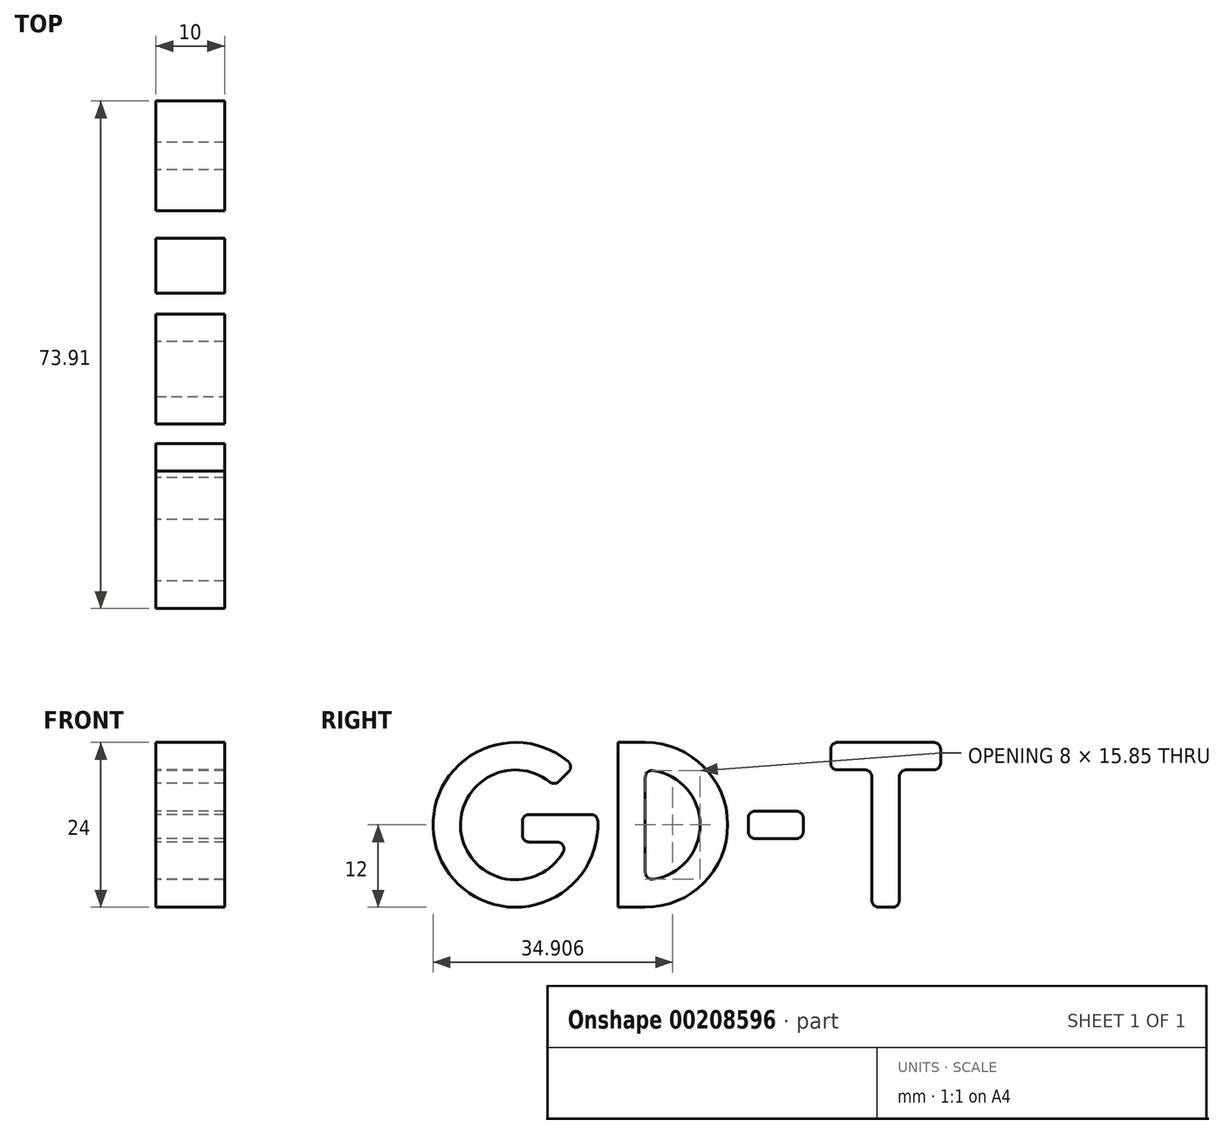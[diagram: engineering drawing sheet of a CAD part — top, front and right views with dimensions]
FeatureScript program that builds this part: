
annotation { "Feature Type Name" : "Feature", "Feature Type Description" : "" }
export const myFeature = defineFeature(function(context is Context, id is Id, definition is map)
    precondition{}
    {
        {
            var Q0;
            Q0=qCreatedBy(makeId("Right.planeOp"),FACE);
            var sketch = newSketch(context, id + "F0", { "sketchPlane" : qUnion([Q0])});
            skArc(sketch, "E0", {"start": v(20.49, 20.49) * mm, "mid": v(1.22, 6.72) * mm, "end": v(23.9, 13.5) * mm});
            skLineSegment(sketch, "E1", {"start": v(23.9, 13.5) * mm, "end": v(13, 13.5) * mm});
            skLineSegment(sketch, "E2", {"start": v(13, 13.5) * mm, "end": v(13, 9.5) * mm});
            skLineSegment(sketch, "E3", {"start": v(13, 9.5) * mm, "end": v(19.6, 9.5) * mm});
            skArc(sketch, "E4", {"start": v(17.66, 17.66) * mm, "mid": v(4.22, 10.15) * mm, "end": v(19.6, 9.5) * mm});
            skLineSegment(sketch, "E5", {"start": v(17.66, 17.66) * mm, "end": v(20.49, 20.49) * mm});
            skArc(sketch, "E6", {"start": v(30.9, 0) * mm, "mid": v(42.9, 12) * mm, "end": v(30.9, 24) * mm});
            skLineSegment(sketch, "E7.bottom", {"start": v(26.9, 0) * mm, "end": v(30.9, 0) * mm});
            skLineSegment(sketch, "E7.top", {"start": v(26.9, 24) * mm, "end": v(30.9, 24) * mm});
            skLineSegment(sketch, "E7.left", {"start": v(26.9, 0) * mm, "end": v(26.9, 24) * mm});
            skArc(sketch, "E8", {"start": v(30.9, 4) * mm, "mid": v(38.9, 12) * mm, "end": v(30.9, 20) * mm});
            skLineSegment(sketch, "E9", {"start": v(30.9, 20) * mm, "end": v(30.9, 4) * mm});
            skLineSegment(sketch, "E10.bottom", {"start": v(45.9, 14) * mm, "end": v(53.9, 14) * mm});
            skLineSegment(sketch, "E10.top", {"start": v(45.9, 10) * mm, "end": v(53.9, 10) * mm});
            skLineSegment(sketch, "E10.left", {"start": v(45.9, 14) * mm, "end": v(45.9, 10) * mm});
            skLineSegment(sketch, "E10.right", {"start": v(53.9, 14) * mm, "end": v(53.9, 10) * mm});
            skLineSegment(sketch, "E11.bottom", {"start": v(57.9, 24) * mm, "end": v(73.9, 24) * mm});
            skLineSegment(sketch, "E11.top", {"start": v(57.9, 20) * mm, "end": v(63.9, 20) * mm});
            skLineSegment(sketch, "E11.left", {"start": v(57.9, 24) * mm, "end": v(57.9, 20) * mm});
            skLineSegment(sketch, "E11.right", {"start": v(73.9, 24) * mm, "end": v(73.9, 20) * mm});
            skLineSegment(sketch, "E12.top", {"start": v(63.9, 0) * mm, "end": v(67.9, 0) * mm});
            skLineSegment(sketch, "E12.left", {"start": v(63.9, 20) * mm, "end": v(63.9, 0) * mm});
            skLineSegment(sketch, "E12.right", {"start": v(67.9, 20) * mm, "end": v(67.9, 0) * mm});
            skLineSegment(sketch, "E13.trimOffspring", {"start": v(67.9, 20) * mm, "end": v(73.9, 20) * mm});
            skSolve(sketch);
        }
        {
            var Q0;
            Q0 = qSketchRegion(id + "F0", true);
            extrude(context, id + "F1", {"entities" : qUnion([Q0]), "depth" : 10 * mm});
        }
        {
            var Q0;
            {var subQ0=sQuery(id+"F0.wireOp",EDGE,"E9");var subQ1=sQuery(id+"F0.wireOp",EDGE,"E8");Q0=makeQuery(id+"F1.opExtrude","SWEPT_EDGE",EDGE,{"disambiguationData":[OSD([subQ1,subQ0]),TDD([makeQuery(id+"F0.imprint","INTERSECT",VERTEX,{"disambiguationData":[OD(1.0)],"derivedFrom":[subQ1,subQ0]})])]});}
            var Q1;
            {var subQ0=sQuery(id+"F0.wireOp",EDGE,"E9");var subQ1=sQuery(id+"F0.wireOp",EDGE,"E8");Q1=makeQuery(id+"F1.opExtrude","SWEPT_EDGE",EDGE,{"disambiguationData":[OSD([subQ1,subQ0]),TDD([makeQuery(id+"F0.imprint","INTERSECT",VERTEX,{"disambiguationData":[OD(0.0)],"derivedFrom":[subQ1,subQ0]})])]});}
            fillet(context, id + "F2", {"entities" : qUnion([Q0, Q1]), "radius" : 1 * mm, "tangentPropagation" : true, "allowEdgeOverflow" : false});
        }
        {
            var Q0;
            Q0=makeQuery(id+"F1.opExtrude","SWEPT_EDGE",EDGE,{"disambiguationData":[OSD([sQuery(id+"F0.wireOp",EDGE,"E3"),sQuery(id+"F0.wireOp",EDGE,"E4")])]});
            var Q1;
            Q1=makeQuery(id+"F1.opExtrude","SWEPT_EDGE",EDGE,{"disambiguationData":[OSD([sQuery(id+"F0.wireOp",EDGE,"E2"),sQuery(id+"F0.wireOp",EDGE,"E3")])]});
            var Q2;
            Q2=makeQuery(id+"F1.opExtrude","SWEPT_EDGE",EDGE,{"disambiguationData":[OSD([sQuery(id+"F0.wireOp",EDGE,"E1"),sQuery(id+"F0.wireOp",EDGE,"E2")])]});
            var Q3;
            Q3=makeQuery(id+"F1.opExtrude","SWEPT_EDGE",EDGE,{"disambiguationData":[OSD([sQuery(id+"F0.wireOp",EDGE,"E0"),sQuery(id+"F0.wireOp",EDGE,"E1")])]});
            var Q4;
            Q4=makeQuery(id+"F1.opExtrude","SWEPT_EDGE",EDGE,{"disambiguationData":[OSD([sQuery(id+"F0.wireOp",EDGE,"E0"),sQuery(id+"F0.wireOp",EDGE,"E5")])]});
            var Q5;
            Q5=makeQuery(id+"F1.opExtrude","SWEPT_EDGE",EDGE,{"disambiguationData":[OSD([sQuery(id+"F0.wireOp",EDGE,"E4"),sQuery(id+"F0.wireOp",EDGE,"E5")])]});
            fillet(context, id + "F3", {"entities" : qUnion([Q0, Q1, Q2, Q3, Q4, Q5]), "radius" : 1 * mm, "tangentPropagation" : true, "allowEdgeOverflow" : false});
        }
        {
            var Q0;
            Q0=makeQuery(id+"F1.opExtrude","SWEPT_EDGE",EDGE,{"disambiguationData":[OSD([sQuery(id+"F0.wireOp",EDGE,"E10.bottom"),sQuery(id+"F0.wireOp",EDGE,"E10.right")])]});
            var Q1;
            Q1=makeQuery(id+"F1.opExtrude","SWEPT_EDGE",EDGE,{"disambiguationData":[OSD([sQuery(id+"F0.wireOp",EDGE,"E10.bottom"),sQuery(id+"F0.wireOp",EDGE,"E10.left")])]});
            var Q2;
            Q2=makeQuery(id+"F1.opExtrude","SWEPT_EDGE",EDGE,{"disambiguationData":[OSD([sQuery(id+"F0.wireOp",EDGE,"E10.top"),sQuery(id+"F0.wireOp",EDGE,"E10.right")])]});
            var Q3;
            Q3=makeQuery(id+"F1.opExtrude","SWEPT_EDGE",EDGE,{"disambiguationData":[OSD([sQuery(id+"F0.wireOp",EDGE,"E10.top"),sQuery(id+"F0.wireOp",EDGE,"E10.left")])]});
            var Q4;
            Q4=makeQuery(id+"F1.opExtrude","SWEPT_EDGE",EDGE,{"disambiguationData":[OSD([sQuery(id+"F0.wireOp",EDGE,"E12.right"),sQuery(id+"F0.wireOp",EDGE,"E13.trimOffspring")])]});
            var Q5;
            Q5=makeQuery(id+"F1.opExtrude","SWEPT_EDGE",EDGE,{"disambiguationData":[OSD([sQuery(id+"F0.wireOp",EDGE,"E11.top"),sQuery(id+"F0.wireOp",EDGE,"E12.left")])]});
            var Q6;
            Q6=makeQuery(id+"F1.opExtrude","SWEPT_EDGE",EDGE,{"disambiguationData":[OSD([sQuery(id+"F0.wireOp",EDGE,"E11.top"),sQuery(id+"F0.wireOp",EDGE,"E11.left")])]});
            var Q7;
            Q7=makeQuery(id+"F1.opExtrude","SWEPT_EDGE",EDGE,{"disambiguationData":[OSD([sQuery(id+"F0.wireOp",EDGE,"E11.bottom"),sQuery(id+"F0.wireOp",EDGE,"E11.left")])]});
            var Q8;
            Q8=makeQuery(id+"F1.opExtrude","SWEPT_EDGE",EDGE,{"disambiguationData":[OSD([sQuery(id+"F0.wireOp",EDGE,"E11.bottom"),sQuery(id+"F0.wireOp",EDGE,"E11.right")])]});
            var Q9;
            Q9=makeQuery(id+"F1.opExtrude","SWEPT_EDGE",EDGE,{"disambiguationData":[OSD([sQuery(id+"F0.wireOp",EDGE,"E11.right"),sQuery(id+"F0.wireOp",EDGE,"E13.trimOffspring")])]});
            var Q10;
            Q10=makeQuery(id+"F1.opExtrude","SWEPT_EDGE",EDGE,{"disambiguationData":[OSD([sQuery(id+"F0.wireOp",EDGE,"E12.top"),sQuery(id+"F0.wireOp",EDGE,"E12.right")])]});
            var Q11;
            Q11=makeQuery(id+"F1.opExtrude","SWEPT_EDGE",EDGE,{"disambiguationData":[OSD([sQuery(id+"F0.wireOp",EDGE,"E12.top"),sQuery(id+"F0.wireOp",EDGE,"E12.left")])]});
            fillet(context, id + "F4", {"entities" : qUnion([Q0, Q1, Q2, Q3, Q4, Q5, Q6, Q7, Q8, Q9, Q10, Q11]), "radius" : 1 * mm, "tangentPropagation" : true, "allowEdgeOverflow" : false});
        }
    });
